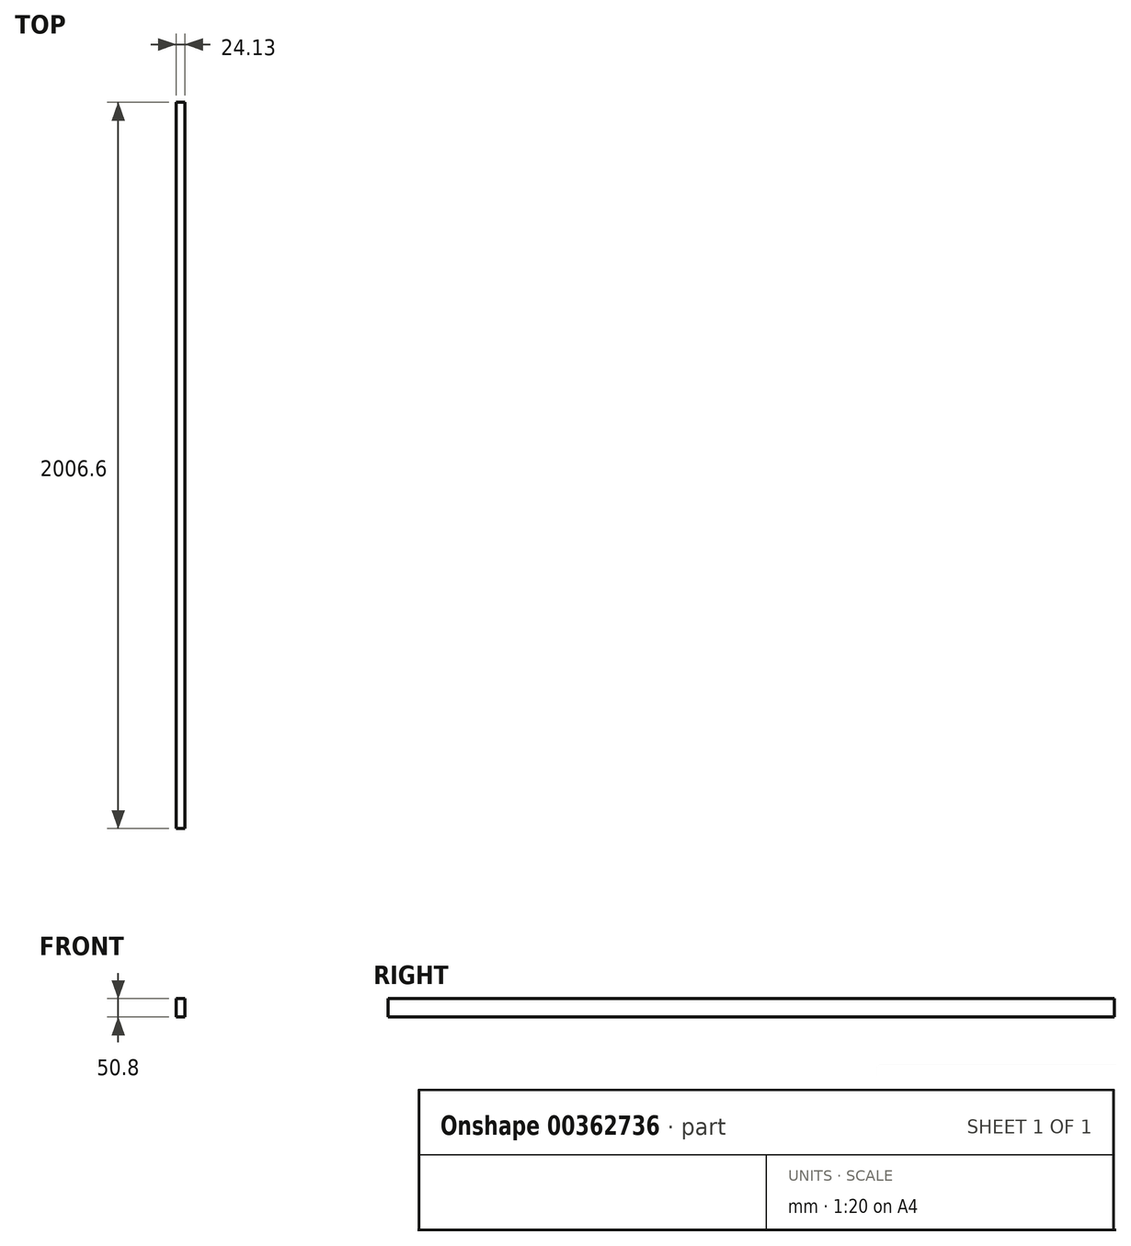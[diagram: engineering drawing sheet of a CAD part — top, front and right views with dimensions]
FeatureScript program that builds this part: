
annotation { "Feature Type Name" : "Feature", "Feature Type Description" : "" }
export const myFeature = defineFeature(function(context is Context, id is Id, definition is map)
    precondition{}
    {
        {
            var Q0;
            Q0=qCreatedBy(makeId("Front.planeOp"),FACE);
            var sketch = newSketch(context, id + "F0", { "sketchPlane" : qUnion([Q0])});
            skLineSegment(sketch, "E0.bottom", {"start": v(-15.21, 30.6) * mm, "end": v(8.92, 30.6) * mm});
            skLineSegment(sketch, "E0.top", {"start": v(-15.21, -20.2) * mm, "end": v(8.92, -20.2) * mm});
            skLineSegment(sketch, "E0.left", {"start": v(-15.21, 30.6) * mm, "end": v(-15.21, -20.2) * mm});
            skLineSegment(sketch, "E0.right", {"start": v(8.92, 30.6) * mm, "end": v(8.92, -20.2) * mm});
            skSolve(sketch);
        }
        {
            var Q0;
            Q0=makeQuery(id+"F0.imprint","IMPRINT",FACE,{"disambiguationData":[TD([[makeQuery(id+"F0.imprint","IMPRINT",EDGE,{"derivedFrom":sQuery(id+"F0.wireOp",EDGE,"E0.bottom")}),-1.0]])]});
            extrude(context, id + "F1", {"entities" : qUnion([Q0]), "depth" : 2006.6 * mm});
        }
    });
